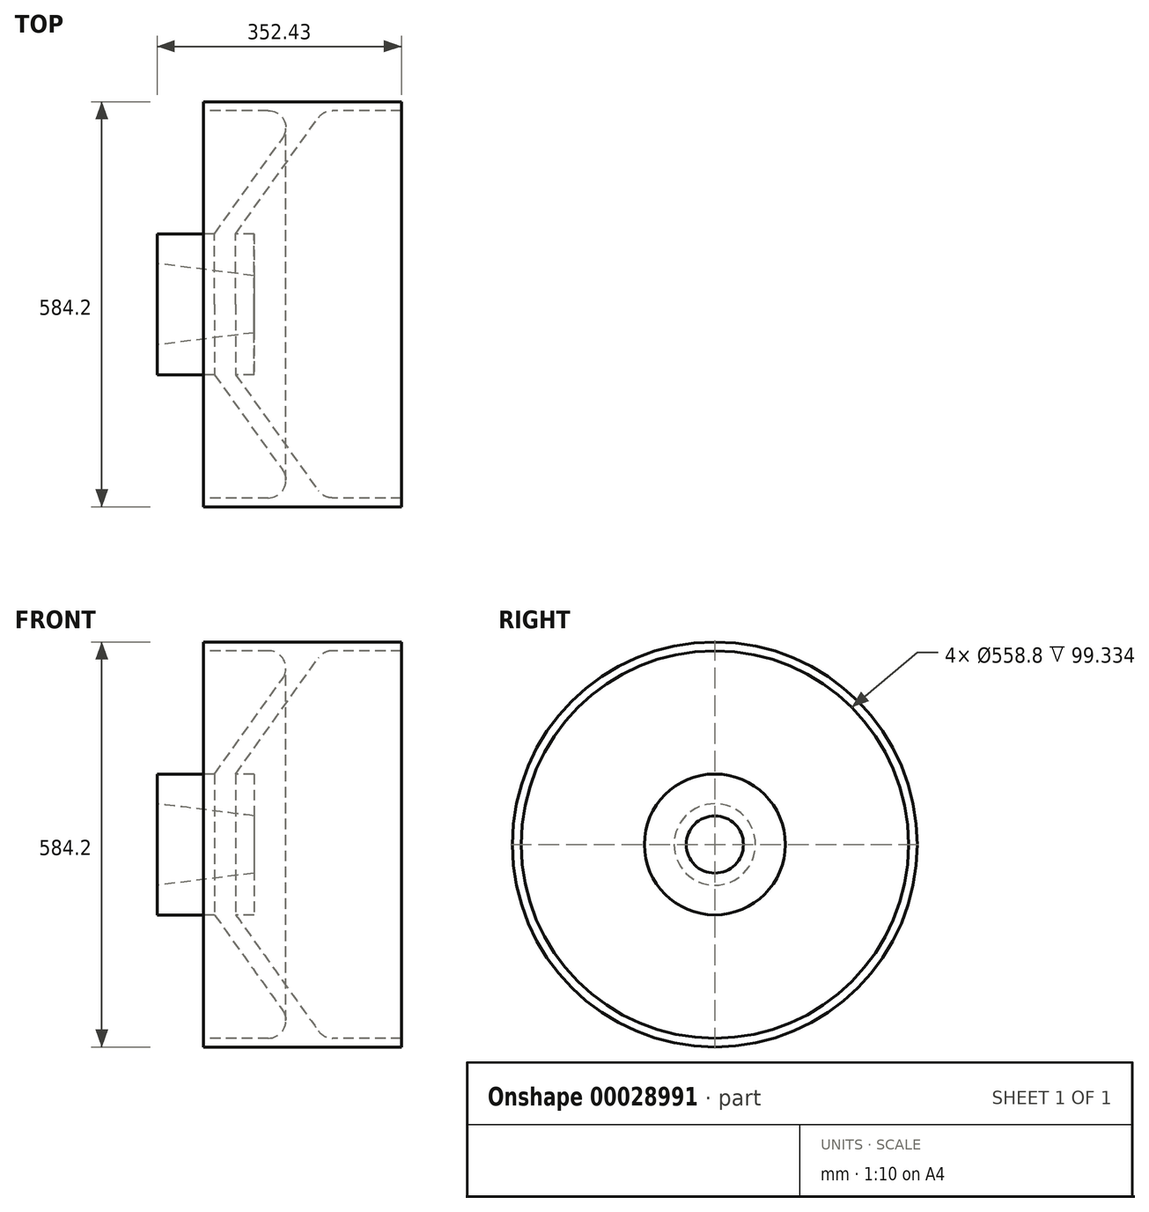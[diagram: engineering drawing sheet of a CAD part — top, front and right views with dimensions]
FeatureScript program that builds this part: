
annotation { "Feature Type Name" : "Feature", "Feature Type Description" : "" }
export const myFeature = defineFeature(function(context is Context, id is Id, definition is map)
    precondition{}
    {
        {
            var Q0;
            Q0=qCreatedBy(makeId("Front.planeOp"),FACE);
            var sketch = newSketch(context, id + "F0", { "sketchPlane" : qUnion([Q0])});
            skLineSegment(sketch, "E0", {"start": v(-118.82, 0) * mm, "end": v(123.9, 0) * mm, "construction": true});
            skLineSegment(sketch, "E1", {"start": v(0, 58.74) * mm, "end": v(0, -75.21) * mm, "construction": true});
            skLineSegment(sketch, "E2.bottom", {"start": v(-142.88, 292.1) * mm, "end": v(142.87, 292.1) * mm});
            skLineSegment(sketch, "E2.top", {"start": v(-142.88, 279.4) * mm, "end": v(142.87, 279.4) * mm});
            skLineSegment(sketch, "E2.left", {"start": v(-142.88, 292.1) * mm, "end": v(-142.88, 279.4) * mm});
            skLineSegment(sketch, "E2.right", {"start": v(142.87, 292.1) * mm, "end": v(142.87, 279.4) * mm});
            skLineSegment(sketch, "E3", {"start": v(0, 279.4) * mm, "end": v(0, 292.1) * mm, "construction": true});
            skLineSegment(sketch, "E4.bottom", {"start": v(-209.55, 101.6) * mm, "end": v(-69.85, 101.6) * mm});
            skLineSegment(sketch, "E4.top", {"start": v(-209.55, 58.74) * mm, "end": v(-69.85, 58.74) * mm});
            skLineSegment(sketch, "E4.left", {"start": v(-209.55, 101.6) * mm, "end": v(-209.55, 58.74) * mm});
            skLineSegment(sketch, "E4.right", {"start": v(-69.85, 101.6) * mm, "end": v(-69.85, 58.74) * mm});
            skLineSegment(sketch, "E5", {"start": v(-96.22, 101.6) * mm, "end": v(30.45, 279.4) * mm});
            skLineSegment(sketch, "E6", {"start": v(0, 279.4) * mm, "end": v(-126.67, 101.6) * mm});
            skLineSegment(sketch, "E7", {"start": v(-69.85, 58.74) * mm, "end": v(-69.85, 41.28) * mm});
            skLineSegment(sketch, "E8", {"start": v(-69.85, 41.27) * mm, "end": v(-209.55, 58.74) * mm});
            skSolve(sketch);
        }
        {
            var Q0;
            Q0=qSketchRegion(id+"F0",true);
            var Q1;
            Q1=sQuery(id+"F0.wireOp",EDGE,"E0");
            revolve(context, id + "F1", {"entities" : qUnion([Q0]), "axis" : qUnion([Q1]), "revolveType" : RevolveType.FULL});
        }
        {
            var Q0;
            Q0=makeQuery(id+"F1.opRevolve","SWEPT_EDGE",EDGE,{"disambiguationData":[OSD([sQuery(id+"F0.wireOp",EDGE,"E2.top"),sQuery(id+"F0.wireOp",EDGE,"E5")])]});
            var Q1;
            Q1=makeQuery(id+"F1.opRevolve","SWEPT_EDGE",EDGE,{"disambiguationData":[OSD([sQuery(id+"F0.wireOp",EDGE,"E2.top"),sQuery(id+"F0.wireOp",EDGE,"E6")])]});
            fillet(context, id + "F2", {"entities" : qUnion([Q0, Q1]), "radius" : 25.4 * mm, "tangentPropagation" : true, "allowEdgeOverflow" : false});
        }
    });
